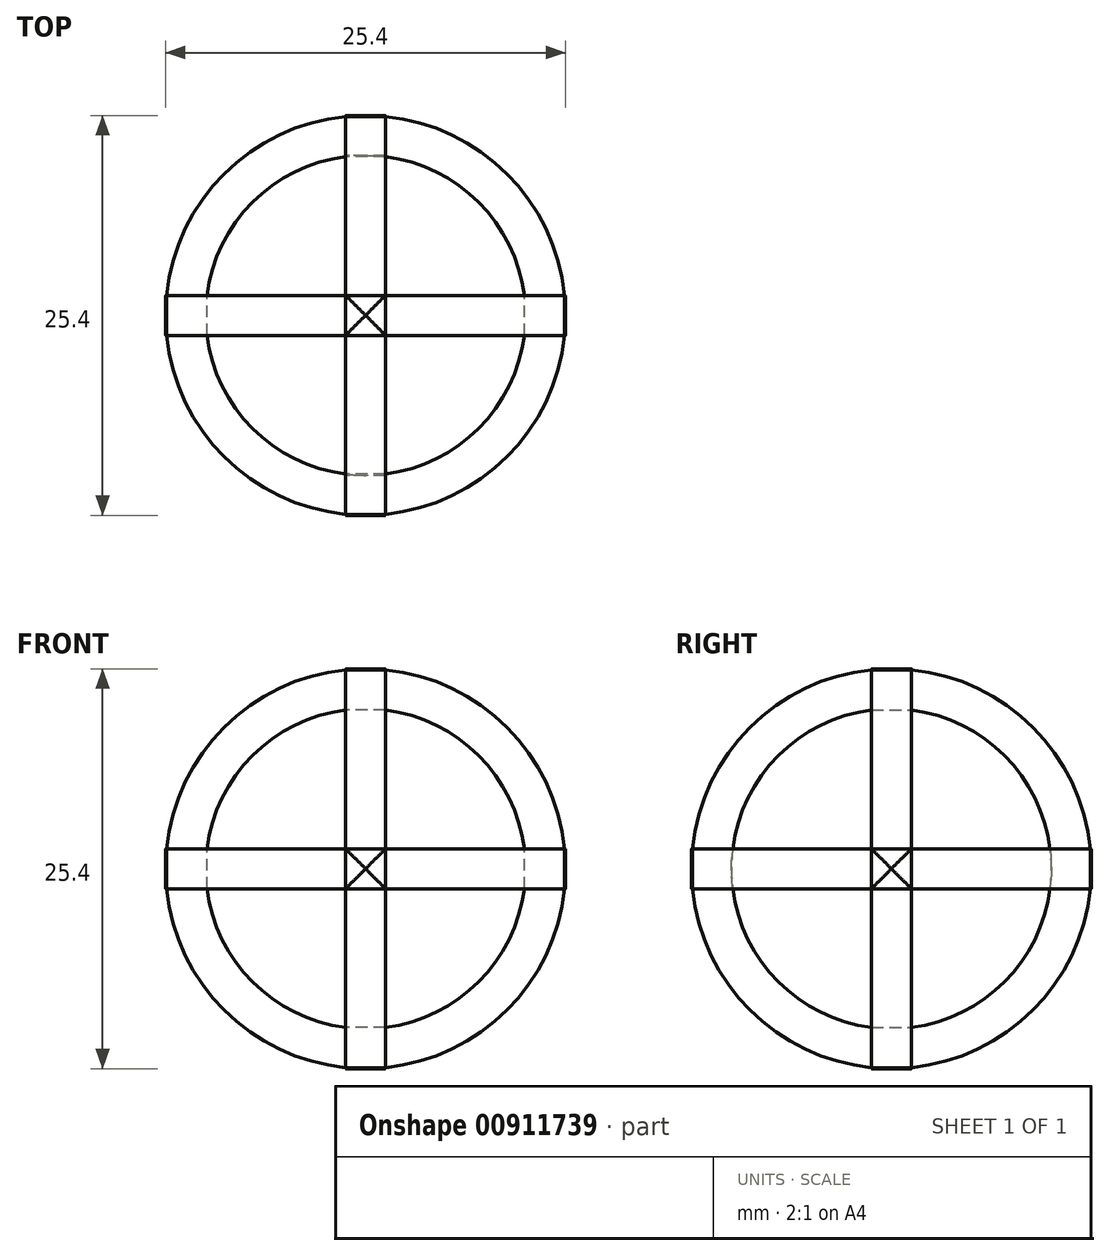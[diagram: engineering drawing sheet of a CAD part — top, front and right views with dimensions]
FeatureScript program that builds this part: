
annotation { "Feature Type Name" : "Feature", "Feature Type Description" : "" }
export const myFeature = defineFeature(function(context is Context, id is Id, definition is map)
    precondition{}
    {
        {
            var Q0;
            Q0=qCreatedBy(makeId("Right.planeOp"),FACE);
            var sketch = newSketch(context, id + "F0", { "sketchPlane" : qUnion([Q0])});
            skCircle(sketch, "E0", {"center": v(0, 0) * mm, "radius": 12.7 * mm});
            skLineSegment(sketch, "E1", {"start": v(-1.27, 1.27) * mm, "end": v(-1.27, 10.08) * mm});
            skLineSegment(sketch, "E2", {"start": v(1.27, 10.08) * mm, "end": v(1.27, 1.27) * mm});
            skLineSegment(sketch, "E3", {"start": v(1.27, 1.27) * mm, "end": v(10.08, 1.27) * mm});
            skLineSegment(sketch, "E4", {"start": v(-1.27, 1.27) * mm, "end": v(-10.08, 1.27) * mm});
            skLineSegment(sketch, "E5", {"start": v(-10.08, -1.27) * mm, "end": v(-1.27, -1.27) * mm});
            skLineSegment(sketch, "E6", {"start": v(-1.27, -1.27) * mm, "end": v(-1.27, -10.08) * mm});
            skLineSegment(sketch, "E7", {"start": v(1.27, -10.08) * mm, "end": v(1.27, -1.27) * mm});
            skLineSegment(sketch, "E8", {"start": v(1.27, -1.27) * mm, "end": v(10.08, -1.27) * mm});
            skCircle(sketch, "E9", {"center": v(0, 0) * mm, "radius": 10.16 * mm});
            skLineSegment(sketch, "E10.bottom", {"start": v(-1.27, -1.27) * mm, "end": v(1.27, -1.27) * mm});
            skLineSegment(sketch, "E10.top", {"start": v(-1.27, 1.27) * mm, "end": v(1.27, 1.27) * mm});
            skLineSegment(sketch, "E10.left", {"start": v(-1.27, -1.27) * mm, "end": v(-1.27, 1.27) * mm});
            skLineSegment(sketch, "E10.right", {"start": v(1.27, -1.27) * mm, "end": v(1.27, 1.27) * mm});
            skSolve(sketch);
        }
        {
            var Q0;
            Q0=makeQuery(id+"F0.imprint","IMPRINT",FACE,{"disambiguationData":[TD([[makeQuery(id+"F0.imprint","IMPRINT",EDGE,{"derivedFrom":sQuery(id+"F0.wireOp",EDGE,"E0")}),1.0]])]});
            extrude(context, id + "F1", {"entities" : qUnion([Q0]), "depth" : 1.27 * mm, "offsetDistance" : 25.4 * mm, "hasSecondDirection" : true, "secondDirectionOppositeDirection" : true, "secondDirectionDepth" : 1.27 * mm});
        }
        {
            var Q0;
            Q0=makeQuery(id+"F0.imprint","IMPRINT",FACE,{"disambiguationData":[TD([[makeQuery(id+"F0.imprint","IMPRINT",EDGE,{"derivedFrom":sQuery(id+"F0.wireOp",EDGE,"E10.bottom")}),1.0]])]});
            extrude(context, id + "F2", {"entities" : qUnion([Q0]), "depth" : 10.16 * mm, "offsetDistance" : 25.4 * mm, "hasSecondDirection" : true, "secondDirectionOppositeDirection" : true, "secondDirectionDepth" : 10.16 * mm});
        }
        {
            var Q0;
            {var subQ0=sQuery(id+"F0.wireOp",EDGE,"E6");Q0=makeQuery(id+"F0.imprint","IMPRINT",FACE,{"disambiguationData":[TD([[makeQuery(id+"F0.imprint","IMPRINT",EDGE,{"derivedFrom":subQ0}),1.0]])]});}
            extrude(context, id + "F3", {"entities" : qUnion([Q0]), "depth" : 1.27 * mm, "offsetDistance" : 25.4 * mm, "hasSecondDirection" : true, "secondDirectionOppositeDirection" : true, "secondDirectionDepth" : 1.27 * mm});
        }
        {
            var Q0;
            {var subQ0=sQuery(id+"F0.wireOp",EDGE,"E3");Q0=makeQuery(id+"F0.imprint","IMPRINT",FACE,{"disambiguationData":[TD([[makeQuery(id+"F0.imprint","IMPRINT",EDGE,{"derivedFrom":subQ0}),-1.0]])]});}
            extrude(context, id + "F4", {"entities" : qUnion([Q0]), "depth" : 1.27 * mm, "offsetDistance" : 25.4 * mm, "hasSecondDirection" : true, "secondDirectionOppositeDirection" : true, "secondDirectionDepth" : 1.27 * mm});
        }
        {
            var Q0;
            {var subQ0=sQuery(id+"F0.wireOp",EDGE,"E4");Q0=makeQuery(id+"F0.imprint","IMPRINT",FACE,{"disambiguationData":[TD([[makeQuery(id+"F0.imprint","IMPRINT",EDGE,{"derivedFrom":subQ0}),1.0]])]});}
            extrude(context, id + "F5", {"entities" : qUnion([Q0]), "depth" : 1.27 * mm, "offsetDistance" : 25.4 * mm, "hasSecondDirection" : true, "secondDirectionOppositeDirection" : true, "secondDirectionDepth" : 1.27 * mm});
        }
        {
            var Q0;
            {var subQ0=sQuery(id+"F0.wireOp",EDGE,"E1");Q0=makeQuery(id+"F0.imprint","IMPRINT",FACE,{"disambiguationData":[TD([[makeQuery(id+"F0.imprint","IMPRINT",EDGE,{"derivedFrom":subQ0}),-1.0]])]});}
            extrude(context, id + "F6", {"entities" : qUnion([Q0]), "depth" : 1.27 * mm, "offsetDistance" : 25.4 * mm, "hasSecondDirection" : true, "secondDirectionOppositeDirection" : true, "secondDirectionDepth" : 1.27 * mm});
        }
        {
            var Q0;
            Q0=makeQuery(id+"F2.opExtrude","SWEPT_FACE",FACE,{"disambiguationData":[OSD([sQuery(id+"F0.wireOp",EDGE,"E10.top")])]});
            var sketch = newSketch(context, id + "F7", { "sketchPlane" : qUnion([Q0])});
            skCircle(sketch, "E11", {"center": v(0, 0) * mm, "radius": 12.7 * mm});
            skCircle(sketch, "E12", {"center": v(0, 0) * mm, "radius": 10.16 * mm});
            skSolve(sketch);
        }
        {
            var Q0;
            Q0 = qSketchRegion(id + "F7", true);
            extrude(context, id + "F8", {"entities" : qUnion([Q0]), "depth" : 0 * mm, "offsetDistance" : 25.4 * mm, "hasSecondDirection" : true, "secondDirectionOppositeDirection" : true, "secondDirectionDepth" : 2.54 * mm});
        }
        {
            var Q0;
            Q0=makeQuery(id+"F3.opExtrude","SWEPT_FACE",FACE,{"disambiguationData":[OSD([sQuery(id+"F0.wireOp",EDGE,"E7")])]});
            var sketch = newSketch(context, id + "F9", { "sketchPlane" : qUnion([Q0])});
            skCircle(sketch, "E13", {"center": v(0, 0) * mm, "radius": 12.7 * mm});
            skCircle(sketch, "E14", {"center": v(0, 0) * mm, "radius": 10.16 * mm});
            skSolve(sketch);
        }
        {
            var Q0;
            Q0 = qSketchRegion(id + "F9", true);
            extrude(context, id + "F10", {"entities" : qUnion([Q0]), "operationType" : NewBodyOperationType.ADD, "depth" : 0 * mm, "offsetDistance" : 25.4 * mm, "hasSecondDirection" : true, "secondDirectionOppositeDirection" : true, "secondDirectionDepth" : 2.54 * mm});
        }
    });
